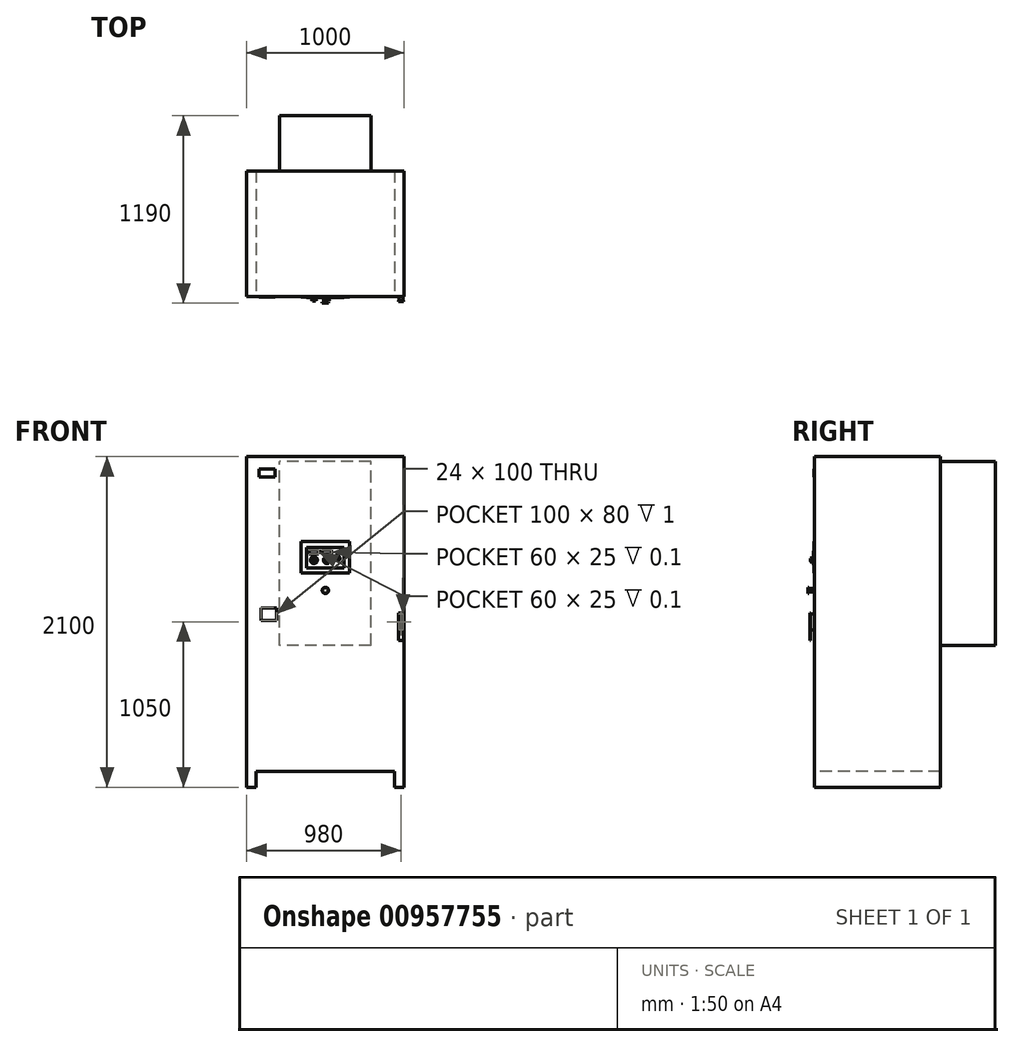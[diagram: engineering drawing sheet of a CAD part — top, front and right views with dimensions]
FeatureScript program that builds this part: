
annotation { "Feature Type Name" : "Feature", "Feature Type Description" : "" }
export const myFeature = defineFeature(function(context is Context, id is Id, definition is map)
    precondition{}
    {
        {
            var Q0;
            Q0=qCreatedBy(makeId("Front.planeOp"),FACE);
            var sketch = newSketch(context, id + "F0", { "sketchPlane" : qUnion([Q0])});
            skLineSegment(sketch, "E0.bottom", {"start": v(500, -1050) * mm, "end": v(-500, -1050) * mm});
            skLineSegment(sketch, "E0.top", {"start": v(500, 1050) * mm, "end": v(-500, 1050) * mm});
            skLineSegment(sketch, "E0.left", {"start": v(500, -1050) * mm, "end": v(500, 1050) * mm});
            skLineSegment(sketch, "E0.right", {"start": v(-500, -1050) * mm, "end": v(-500, 1050) * mm});
            skPoint(sketch, "E0.middle", {"position": v(0, 0) * mm});
            skSolve(sketch);
        }
        {
            var Q0;
            Q0 = qSketchRegion(id + "F0", true);
            extrude(context, id + "F1", {"entities" : qUnion([Q0]), "oppositeDirection" : true, "depth" : 800 * mm, "offsetDistance" : 25 * mm});
        }
        {
            var Q0;
            Q0=makeQuery(id+"F1.opExtrude","CAP_FACE",FACE,{"disambiguationData":[OSD([sQuery(id+"F0.wireOp",EDGE,"E0.bottom"),sQuery(id+"F0.wireOp",EDGE,"E0.top"),sQuery(id+"F0.wireOp",EDGE,"E0.left"),sQuery(id+"F0.wireOp",EDGE,"E0.right")])],"isStart":false});
            var sketch = newSketch(context, id + "F2", { "sketchPlane" : qUnion([Q0])});
            skLineSegment(sketch, "E1.bottom", {"start": v(-290, -150) * mm, "end": v(290, -150) * mm});
            skLineSegment(sketch, "E1.top", {"start": v(-290, 1020) * mm, "end": v(290, 1020) * mm});
            skLineSegment(sketch, "E1.left", {"start": v(-290, -150) * mm, "end": v(-290, 1020) * mm});
            skLineSegment(sketch, "E1.right", {"start": v(290, -150) * mm, "end": v(290, 1020) * mm});
            skPoint(sketch, "E1.middle", {"position": v(0, 435) * mm});
            skSolve(sketch);
        }
        {
            var Q0;
            Q0 = qSketchRegion(id + "F2", true);
            extrude(context, id + "F3", {"entities" : qUnion([Q0]), "operationType" : NewBodyOperationType.ADD, "depth" : (1150 - 800) * mm, "offsetDistance" : 25 * mm});
        }
        {
            var Q0;
            Q0=makeQuery(id+"F1.opExtrude","CAP_FACE",FACE,{"disambiguationData":[OSD([sQuery(id+"F0.wireOp",EDGE,"E0.bottom"),sQuery(id+"F0.wireOp",EDGE,"E0.top"),sQuery(id+"F0.wireOp",EDGE,"E0.left"),sQuery(id+"F0.wireOp",EDGE,"E0.right")])],"isStart":true});
            var sketch = newSketch(context, id + "F4", { "sketchPlane" : qUnion([Q0])});
            skCircle(sketch, "E2", {"center": v(0, 200) * mm, "radius": 11 * mm});
            skSolve(sketch);
        }
        {
            var Q0;
            Q0 = qSketchRegion(id + "F4", true);
            extrude(context, id + "F5", {"entities" : qUnion([Q0]), "operationType" : NewBodyOperationType.ADD, "depth" : 40 * mm, "offsetDistance" : 25 * mm});
        }
        {
            var Q0;
            Q0=makeQuery(id+"F5.opExtrude","CAP_FACE",FACE,{"disambiguationData":[OSD([sQuery(id+"F4.wireOp",EDGE,"E2")])],"isStart":false});
            var sketch = newSketch(context, id + "F6", { "sketchPlane" : qUnion([Q0])});
            skCircle(sketch, "E3", {"center": v(0, 200) * mm, "radius": 20 * mm});
            skSolve(sketch);
        }
        {
            var Q0;
            Q0 = qSketchRegion(id + "F6", true);
            extrude(context, id + "F7", {"entities" : qUnion([Q0]), "operationType" : NewBodyOperationType.ADD, "oppositeDirection" : true, "depth" : 5 * mm, "offsetDistance" : 25 * mm});
        }
        {
            var Q0;
            Q0=makeQuery(id+"F1.opExtrude","CAP_FACE",FACE,{"disambiguationData":[OSD([sQuery(id+"F0.wireOp",EDGE,"E0.bottom"),sQuery(id+"F0.wireOp",EDGE,"E0.top"),sQuery(id+"F0.wireOp",EDGE,"E0.left"),sQuery(id+"F0.wireOp",EDGE,"E0.right")])],"isStart":true});
            var sketch = newSketch(context, id + "F8", { "sketchPlane" : qUnion([Q0])});
            skLineSegment(sketch, "E4.bottom", {"start": v(155, 310) * mm, "end": v(-155, 310) * mm});
            skLineSegment(sketch, "E4.top", {"start": v(155, 510) * mm, "end": v(-155, 510) * mm});
            skLineSegment(sketch, "E4.left", {"start": v(155, 310) * mm, "end": v(155, 510) * mm});
            skLineSegment(sketch, "E4.right", {"start": v(-155, 310) * mm, "end": v(-155, 510) * mm});
            skPoint(sketch, "E4.middle", {"position": v(0, 410) * mm});
            skSolve(sketch);
        }
        {
            var Q0;
            Q0 = qSketchRegion(id + "F8", true);
            extrude(context, id + "F9", {"entities" : qUnion([Q0]), "operationType" : NewBodyOperationType.ADD, "depth" : 3 * mm, "offsetDistance" : 25 * mm});
        }
        {
            var Q0;
            Q0=makeQuery(id+"F1.opExtrude","CAP_FACE",FACE,{"disambiguationData":[OSD([sQuery(id+"F0.wireOp",EDGE,"E0.bottom"),sQuery(id+"F0.wireOp",EDGE,"E0.top"),sQuery(id+"F0.wireOp",EDGE,"E0.left"),sQuery(id+"F0.wireOp",EDGE,"E0.right")])],"isStart":true});
            var sketch = newSketch(context, id + "F10", { "sketchPlane" : qUnion([Q0])});
            skLineSegment(sketch, "E5.bottom", {"start": v(-310, 10) * mm, "end": v(-410, 10) * mm});
            skLineSegment(sketch, "E5.top", {"start": v(-310, 90) * mm, "end": v(-410, 90) * mm});
            skLineSegment(sketch, "E5.left", {"start": v(-310, 10) * mm, "end": v(-310, 90) * mm});
            skLineSegment(sketch, "E5.right", {"start": v(-410, 10) * mm, "end": v(-410, 90) * mm});
            skPoint(sketch, "E5.middle", {"position": v(-360, 50) * mm});
            skSolve(sketch);
        }
        {
            var Q0;
            Q0 = qSketchRegion(id + "F10", true);
            extrude(context, id + "F11", {"entities" : qUnion([Q0]), "operationType" : NewBodyOperationType.REMOVE, "oppositeDirection" : true, "depth" : 1 * mm, "offsetDistance" : 25 * mm});
        }
        {
            var Q0;
            Q0=makeQuery(id+"F1.opExtrude","CAP_FACE",FACE,{"disambiguationData":[OSD([sQuery(id+"F0.wireOp",EDGE,"E0.bottom"),sQuery(id+"F0.wireOp",EDGE,"E0.top"),sQuery(id+"F0.wireOp",EDGE,"E0.left"),sQuery(id+"F0.wireOp",EDGE,"E0.right")])],"isStart":true});
            var sketch = newSketch(context, id + "F12", { "sketchPlane" : qUnion([Q0])});
            skLineSegment(sketch, "E6.bottom", {"start": v(-440, -1050) * mm, "end": v(440, -1050) * mm});
            skLineSegment(sketch, "E6.top", {"start": v(-440, -950) * mm, "end": v(440, -950) * mm});
            skLineSegment(sketch, "E6.left", {"start": v(-440, -1050) * mm, "end": v(-440, -950) * mm});
            skLineSegment(sketch, "E6.right", {"start": v(440, -1050) * mm, "end": v(440, -950) * mm});
            skSolve(sketch);
        }
        {
            var Q0;
            Q0 = qSketchRegion(id + "F12", true);
            extrude(context, id + "F13", {"entities" : qUnion([Q0]), "operationType" : NewBodyOperationType.REMOVE, "endBound" : BoundingType.THROUGH_ALL, "oppositeDirection" : true, "depth" : 25 * mm, "offsetDistance" : 25 * mm});
        }
        {
            var Q0;
            Q0=makeQuery(id+"F1.opExtrude","CAP_FACE",FACE,{"disambiguationData":[OSD([sQuery(id+"F0.wireOp",EDGE,"E0.bottom"),sQuery(id+"F0.wireOp",EDGE,"E0.top"),sQuery(id+"F0.wireOp",EDGE,"E0.left"),sQuery(id+"F0.wireOp",EDGE,"E0.right")])],"isStart":true});
            var sketch = newSketch(context, id + "F14", { "sketchPlane" : qUnion([Q0])});
            skLineSegment(sketch, "E7.bottom", {"start": v(492, -50) * mm, "end": v(468, -50) * mm});
            skLineSegment(sketch, "E7.top", {"start": v(492, 50) * mm, "end": v(468, 50) * mm});
            skLineSegment(sketch, "E7.left", {"start": v(492, -50) * mm, "end": v(492, 50) * mm});
            skLineSegment(sketch, "E7.right", {"start": v(468, -50) * mm, "end": v(468, 50) * mm});
            skPoint(sketch, "E7.middle", {"position": v(480, 0) * mm});
            skSolve(sketch);
        }
        {
            var Q0;
            Q0 = qSketchRegion(id + "F14", true);
            extrude(context, id + "F15", {"entities" : qUnion([Q0]), "operationType" : NewBodyOperationType.ADD, "depth" : 25 * mm, "offsetDistance" : 25 * mm});
        }
        {
            var Q0;
            Q0=makeQuery(id+"F1.opExtrude","CAP_FACE",FACE,{"disambiguationData":[OSD([sQuery(id+"F0.wireOp",EDGE,"E0.bottom"),sQuery(id+"F0.wireOp",EDGE,"E0.top"),sQuery(id+"F0.wireOp",EDGE,"E0.left"),sQuery(id+"F0.wireOp",EDGE,"E0.right")])],"isStart":true});
            var sketch = newSketch(context, id + "F16", { "sketchPlane" : qUnion([Q0])});
            skLineSegment(sketch, "E8.bottom", {"start": v(-320, 920) * mm, "end": v(-420, 920) * mm});
            skLineSegment(sketch, "E8.top", {"start": v(-320, 970) * mm, "end": v(-420, 970) * mm});
            skLineSegment(sketch, "E8.left", {"start": v(-320, 920) * mm, "end": v(-320, 970) * mm});
            skLineSegment(sketch, "E8.right", {"start": v(-420, 920) * mm, "end": v(-420, 970) * mm});
            skPoint(sketch, "E8.middle", {"position": v(-370, 945) * mm});
            skSolve(sketch);
        }
        {
            var Q0;
            Q0 = qSketchRegion(id + "F16", true);
            extrude(context, id + "F17", {"entities" : qUnion([Q0]), "operationType" : NewBodyOperationType.ADD, "depth" : 2 * mm, "offsetDistance" : 25 * mm});
        }
        {
            var Q0;
            Q0=makeQuery(id+"F15.opExtrude","CAP_FACE",FACE,{"disambiguationData":[OSD([sQuery(id+"F14.wireOp",EDGE,"E7.bottom"),sQuery(id+"F14.wireOp",EDGE,"E7.top"),sQuery(id+"F14.wireOp",EDGE,"E7.left"),sQuery(id+"F14.wireOp",EDGE,"E7.right")])],"isStart":false});
            var sketch = newSketch(context, id + "F18", { "sketchPlane" : qUnion([Q0])});
            skLineSegment(sketch, "E9.bottom", {"start": v(495, -117) * mm, "end": v(465, -117) * mm});
            skLineSegment(sketch, "E9.top", {"start": v(495, 58) * mm, "end": v(465, 58) * mm});
            skLineSegment(sketch, "E9.left", {"start": v(495, -117) * mm, "end": v(495, 58) * mm});
            skLineSegment(sketch, "E9.right", {"start": v(465, -117) * mm, "end": v(465, 58) * mm});
            skPoint(sketch, "E9.middle", {"position": v(480, -29.5) * mm});
            skPoint(sketch, "E9.middle.positionSnap0", {"position": v(480, -50) * mm});
            skPoint(sketch, "E9.centerSnap0", {"position": v(480, -50) * mm});
            skSolve(sketch);
        }
        {
            var Q0;
            Q0 = qSketchRegion(id + "F18", true);
            extrude(context, id + "F19", {"entities" : qUnion([Q0]), "operationType" : NewBodyOperationType.ADD, "depth" : 4 * mm, "offsetDistance" : 25 * mm});
        }
        {
            var Q0;
            Q0=makeQuery(id+"F9.opExtrude","CAP_FACE",FACE,{"disambiguationData":[OSD([sQuery(id+"F8.wireOp",EDGE,"E4.bottom"),sQuery(id+"F8.wireOp",EDGE,"E4.top"),sQuery(id+"F8.wireOp",EDGE,"E4.left"),sQuery(id+"F8.wireOp",EDGE,"E4.right")])],"isStart":false});
            var sketch = newSketch(context, id + "F20", { "sketchPlane" : qUnion([Q0])});
            skLineSegment(sketch, "E10.bottom", {"start": v(120, 343) * mm, "end": v(-120, 343) * mm});
            skLineSegment(sketch, "E10.top", {"start": v(120, 473) * mm, "end": v(-120, 473) * mm});
            skLineSegment(sketch, "E10.left", {"start": v(120, 343) * mm, "end": v(120, 473) * mm});
            skLineSegment(sketch, "E10.right", {"start": v(-120, 343) * mm, "end": v(-120, 473) * mm});
            skPoint(sketch, "E10.middle", {"position": v(0, 408) * mm});
            skSolve(sketch);
        }
        {
            var Q0;
            Q0 = qSketchRegion(id + "F20", true);
            extrude(context, id + "F21", {"entities" : qUnion([Q0]), "operationType" : NewBodyOperationType.ADD, "depth" : 1 * mm, "offsetDistance" : 25 * mm});
        }
        {
            var Q0;
            Q0=makeQuery(id+"F21.opExtrude","CAP_FACE",FACE,{"disambiguationData":[OSD([sQuery(id+"F20.wireOp",EDGE,"E10.bottom"),sQuery(id+"F20.wireOp",EDGE,"E10.top"),sQuery(id+"F20.wireOp",EDGE,"E10.left"),sQuery(id+"F20.wireOp",EDGE,"E10.right")])],"isStart":false});
            var sketch = newSketch(context, id + "F22", { "sketchPlane" : qUnion([Q0])});
            skLineSegment(sketch, "E11.bottom", {"start": v(-43, 432) * mm, "end": v(-103, 432) * mm});
            skLineSegment(sketch, "E11.top", {"start": v(-43, 457) * mm, "end": v(-103, 457) * mm});
            skLineSegment(sketch, "E11.left", {"start": v(-43, 432) * mm, "end": v(-43, 457) * mm});
            skLineSegment(sketch, "E11.right", {"start": v(-103, 432) * mm, "end": v(-103, 457) * mm});
            skPoint(sketch, "E11.middle", {"position": v(-73, 444.5) * mm});
            skLineSegment(sketch, "E12.bottom", {"start": v(40, 432) * mm, "end": v(-20, 432) * mm});
            skLineSegment(sketch, "E12.top", {"start": v(40, 457) * mm, "end": v(-20, 457) * mm});
            skLineSegment(sketch, "E12.left", {"start": v(40, 432) * mm, "end": v(40, 457) * mm});
            skLineSegment(sketch, "E12.right", {"start": v(-20, 432) * mm, "end": v(-20, 457) * mm});
            skPoint(sketch, "E12.middle", {"position": v(10, 444.5) * mm});
            skSolve(sketch);
        }
        {
            var Q0;
            Q0 = qSketchRegion(id + "F22", true);
            extrude(context, id + "F23", {"entities" : qUnion([Q0]), "operationType" : NewBodyOperationType.REMOVE, "oppositeDirection" : true, "depth" : 0.1 * mm, "offsetDistance" : 25 * mm});
        }
        {
            var Q0;
            Q0=makeQuery(id+"F21.opExtrude","CAP_FACE",FACE,{"disambiguationData":[OSD([sQuery(id+"F20.wireOp",EDGE,"E10.bottom"),sQuery(id+"F20.wireOp",EDGE,"E10.top"),sQuery(id+"F20.wireOp",EDGE,"E10.left"),sQuery(id+"F20.wireOp",EDGE,"E10.right")])],"isStart":false});
            var sketch = newSketch(context, id + "F24", { "sketchPlane" : qUnion([Q0])});
            skCircle(sketch, "E13", {"center": v(-73, 393) * mm, "radius": 22.5 * mm});
            skCircle(sketch, "E14", {"center": v(10, 393) * mm, "radius": 22.5 * mm});
            skPoint(sketch, "E15", {"position": v(-73, 432) * mm});
            skPoint(sketch, "E16", {"position": v(10, 432) * mm});
            skSolve(sketch);
        }
        {
            var Q0;
            Q0=sQuery(id+"F24.wireOp",VERTEX,"E13.center");
            var Q1;
            Q1=makeQuery(id+"F9.opExtrude","SWEPT_FACE",FACE,{"disambiguationData":[OSD([sQuery(id+"F8.wireOp",EDGE,"E4.bottom")])]});
            cPlane(context, id + "F25", {"entities" : qUnion([Q0, Q1]), "cplaneType" : CPlaneType.PLANE_POINT, "offset" : 25 * mm, "width" : 150 * mm, "height" : 150 * mm});
        }
        {
            var Q0;
            Q0=qCreatedBy(id+"F25.planeOp",FACE);
            var sketch = newSketch(context, id + "F26", { "sketchPlane" : qUnion([Q0])});
            skPoint(sketch, "E17", {"position": v(-73, 4) * mm});
            skLineSegment(sketch, "E18", {"start": v(-73, 4) * mm, "end": v(-73, 26) * mm});
            skLineSegment(sketch, "E19", {"start": v(-73, 26) * mm, "end": v(-83, 26) * mm});
            skLineSegment(sketch, "E20", {"start": v(-83, 26) * mm, "end": v(-85, 16) * mm});
            skLineSegment(sketch, "E21", {"start": v(-85, 16) * mm, "end": v(-95.5, 14) * mm});
            skLineSegment(sketch, "E22", {"start": v(-95.5, 14) * mm, "end": v(-95.5, 4) * mm});
            skLineSegment(sketch, "E23", {"start": v(-95.5, 4) * mm, "end": v(-73, 4) * mm});
            skLineSegment(sketch, "E24", {"start": v(-73, 45.66) * mm, "end": v(-73, -10.72) * mm, "construction": true});
            skPoint(sketch, "E25", {"position": v(10, 4) * mm});
            skLineSegment(sketch, "E26", {"start": v(10, 42.44) * mm, "end": v(10, -16.58) * mm, "construction": true});
            skLineSegment(sketch, "E27", {"start": v(10, 4) * mm, "end": v(-12.5, 4) * mm});
            skLineSegment(sketch, "E28", {"start": v(-12.5, 4) * mm, "end": v(-12.5, 14) * mm});
            skLineSegment(sketch, "E29", {"start": v(-12.5, 14) * mm, "end": v(-2, 16) * mm});
            skLineSegment(sketch, "E30", {"start": v(-2, 16) * mm, "end": v(0, 26) * mm});
            skLineSegment(sketch, "E31", {"start": v(0, 26) * mm, "end": v(10, 26) * mm});
            skLineSegment(sketch, "E32", {"start": v(10, 26) * mm, "end": v(10, 4) * mm});
            skSolve(sketch);
        }
        {
            var Q0;
            Q0=makeQuery(id+"F26.imprint","IMPRINT",FACE,{"disambiguationData":[TD([[makeQuery(id+"F26.imprint","IMPRINT",EDGE,{"derivedFrom":sQuery(id+"F26.wireOp",EDGE,"E18")}),1.0]])]});
            var Q1;
            Q1=sQuery(id+"F26.wireOp",EDGE,"E24");
            revolve(context, id + "F27", {"operationType" : NewBodyOperationType.ADD, "surfaceOperationType" : NewSurfaceOperationType.NEW, "entities" : qUnion([Q0]), "axis" : qUnion([Q1]), "revolveType" : RevolveType.FULL});
        }
        {
            var Q0;
            Q0=makeQuery(id+"F26.imprint","IMPRINT",FACE,{"disambiguationData":[TD([[makeQuery(id+"F26.imprint","IMPRINT",EDGE,{"derivedFrom":sQuery(id+"F26.wireOp",EDGE,"E27")}),-1.0]])]});
            var Q1;
            Q1=sQuery(id+"F26.wireOp",EDGE,"E26");
            revolve(context, id + "F28", {"operationType" : NewBodyOperationType.ADD, "surfaceOperationType" : NewSurfaceOperationType.NEW, "entities" : qUnion([Q0]), "axis" : qUnion([Q1]), "revolveType" : RevolveType.FULL});
        }
        {
            var Q0;
            Q0=makeQuery(id+"F24.imprint","IMPRINT",FACE,{"disambiguationData":[TD([[makeQuery(id+"F24.imprint","IMPRINT",EDGE,{"derivedFrom":sQuery(id+"F24.wireOp",EDGE,"E13")}),-1.0]])]});
            var sketch = newSketch(context, id + "F29", { "sketchPlane" : qUnion([Q0])});
            skCircle(sketch, "E33", {"center": v(83.55, 438) * mm, "radius": 11 * mm});
            skCircle(sketch, "E34", {"center": v(83.55, 403) * mm, "radius": 11 * mm});
            skSolve(sketch);
        }
        {
            var Q0;
            Q0 = qSketchRegion(id + "F29", true);
            extrude(context, id + "F30", {"entities" : qUnion([Q0]), "operationType" : NewBodyOperationType.ADD, "depth" : 1 * mm, "offsetDistance" : 25 * mm});
        }
    });
